# Revit family: HOB_GEN_Symphony_Opera_5
name_source: partatom
category: Generic Models
units: mm (PartAtom-declared; Revit-internal decimal feet)

## family parameters
Always vertical = Yes
Can host rebar = No
Cut with Voids When Loaded = No
Maintain Annotation Orientation = No
Part Type = Normal
Room Calculation Point = No
Round Connector Dimension = Use Diameter
Shared = Yes
Work Plane-Based = No

## types (1)
- HOB_GEN_Symphony_Opera_5
    ArrayLength = 1176 mm  [stored 3.85827 ft]
    ArrayNumberLength = 74
    ArrayNumberWidth = 36
    ArrayWidth = 576 mm  [stored 1.88976 ft]
    Default Elevation = 0 mm  [stored 0 ft]
    HolesRadius = 2 mm  [stored 0.00656168 ft]
    Length = 1200 mm  [stored 3.93701 ft]
    Material = Bamboo_horizontalGrain
    SectionArea = 0 m²
    SideOffset = 12 mm  [stored 0.0393701 ft]
    Width = 600 mm  [stored 1.9685 ft]

note: [stored X ft] marks values corroborated as IEEE doubles in the binary element streams (Revit-internal decimal feet)

## geometry (parser evidence)
native form markers: Sweep x2
no freeform markers — native parametric forms only
